# Revit family: URANUS_60W_4000K_5580LM_800DIAM
name_source: partatom
category: Lighting Fixtures
units: mm (PartAtom-declared; Revit-internal decimal feet)

## family parameters
Always vertical = Yes
Cut with Voids When Loaded = No
Host = Ceiling
Light Source = Yes
OmniClass Number = 23.80.70.11
OmniClass Title = Luminaries for Internal Lighting
Part Type = Normal
Room Calculation Point = No
Round Connector Dimension = Use Diameter
Shared = No

## types (1)
- Type 1
    Alimentation Driver = AC 200-240 V
    Alimentation luminaire = 1500mA / 27-42V
    Angle d'éclairage = 120°
    Color Filter = 16777215
    Default Elevation = 0 mm  [stored 0 ft]
    Dimensions = ø 800 mm; H : 20 mm
    Dimming Lamp Color Temperature Shift = <None>
    Driver = Driver Lifud
    Durée de vie = 50 000 heures
    Emit Shape Visible in Rendering = No
    Emit from Circle Diameter = 610 mm
    Fintion = Blanc texturé
    IRC = >80
    Longueur filins de suspension = 1900 mm
    Matériau = Aluminium
    Photometric Web File = google_eulumdat_converter (12).ies
    Puissance nominale = 60W
    Tilt Angle = 90.00°
    Type = Suspension
    Type de lampe = SMD 2835 LM-80

note: [stored X ft] marks values corroborated as IEEE doubles in the binary element streams (Revit-internal decimal feet)

## geometry (parser evidence)
native form markers: Sweep x3
no freeform markers — native parametric forms only
